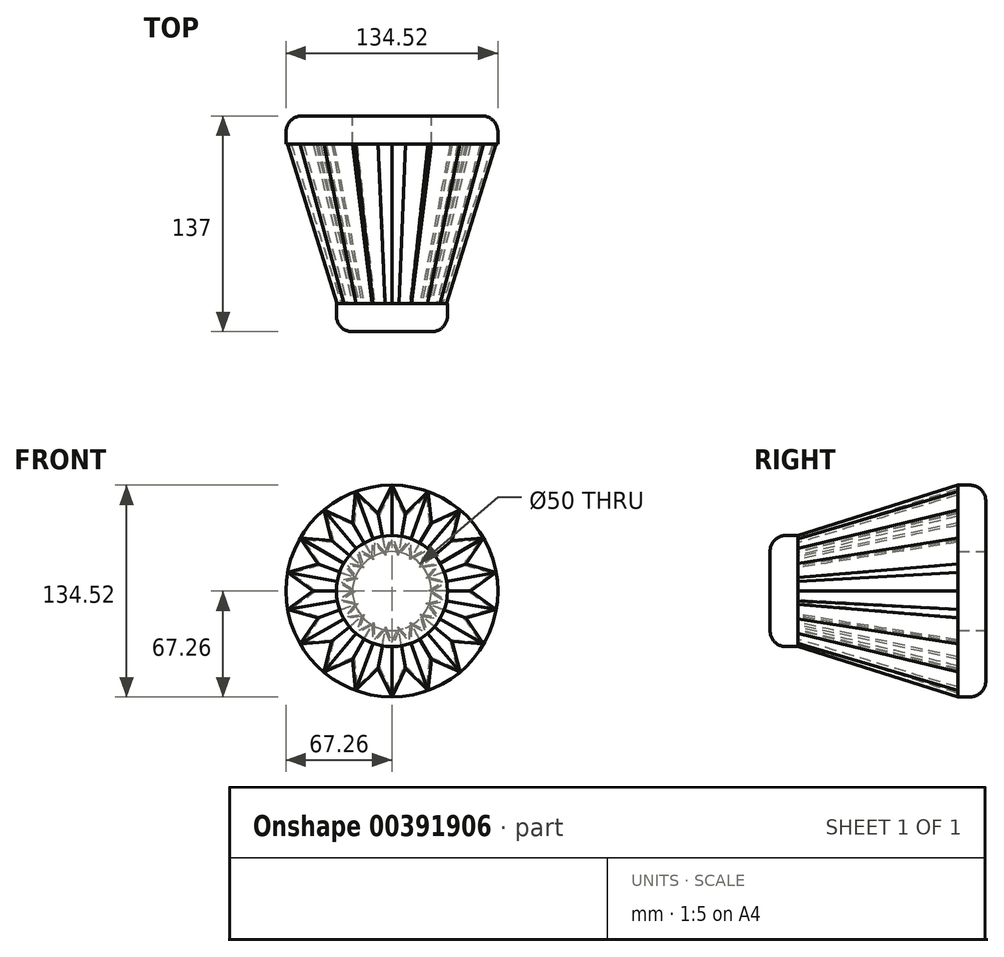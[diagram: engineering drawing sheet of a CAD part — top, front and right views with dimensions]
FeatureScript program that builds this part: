
annotation { "Feature Type Name" : "Feature", "Feature Type Description" : "" }
export const myFeature = defineFeature(function(context is Context, id is Id, definition is map)
    precondition{}
    {
        {
            var Q0;
            Q0=qCreatedBy(makeId("Front.planeOp"),FACE);
            var sketch = newSketch(context, id + "F0", { "sketchPlane" : qUnion([Q0])});
            skLineSegment(sketch, "E0", {"start": v(0, 0) * mm, "end": v(0, 67.26) * mm, "construction": true});
            skLineSegment(sketch, "E1", {"start": v(0, 0) * mm, "end": v(-8.68, 49.24) * mm});
            skLineSegment(sketch, "E2", {"start": v(-8.68, 49.24) * mm, "end": v(0, 67.26) * mm});
            skLineSegment(sketch, "E3.MirrorCS", {"start": v(8.68, 49.24) * mm, "end": v(0, 67.26) * mm});
            skLineSegment(sketch, "E4.MirrorCS", {"start": v(0, 0) * mm, "end": v(8.68, 49.24) * mm});
            skSolve(sketch);
        }
        {
            var Q0;
            Q0=qCreatedBy(makeId("Front.planeOp"),FACE);
            cPlane(context, id + "F1", {"entities" : qUnion([Q0]), "cplaneType" : CPlaneType.OFFSET, "offset" : 101.5 * mm, "width" : 150 * mm, "height" : 150 * mm});
        }
        {
            var Q0;
            Q0=qCreatedBy(id+"F1.planeOp",FACE);
            var sketch = newSketch(context, id + "F2", { "sketchPlane" : qUnion([Q0])});
            skLineSegment(sketch, "E5", {"start": v(0, 0) * mm, "end": v(0, 49.56) * mm, "construction": true});
            skLineSegment(sketch, "E6", {"start": v(0, 0) * mm, "end": v(-4.34, 24.62) * mm});
            skLineSegment(sketch, "E7", {"start": v(-4.34, 24.62) * mm, "end": v(0, 35.27) * mm});
            skLineSegment(sketch, "E8.MirrorCS", {"start": v(4.34, 24.62) * mm, "end": v(0, 35.27) * mm});
            skLineSegment(sketch, "E9.MirrorCS", {"start": v(0, 0) * mm, "end": v(4.34, 24.62) * mm});
            skSolve(sketch);
        }
        {
            var Q0;
            Q0=makeQuery(id+"F0.imprint","IMPRINT",FACE,{"disambiguationData":[TD([[makeQuery(id+"F0.imprint","IMPRINT",EDGE,{"derivedFrom":sQuery(id+"F0.wireOp",EDGE,"E1")}),-1.0]])]});
            var Q1;
            Q1=makeQuery(id+"F2.imprint","IMPRINT",FACE,{"disambiguationData":[TD([[makeQuery(id+"F2.imprint","IMPRINT",EDGE,{"derivedFrom":sQuery(id+"F2.wireOp",EDGE,"E6")}),-1.0]])]});
            loft(context, id + "F3", {"sheetProfilesArray" : [{ "sheetProfileEntities" : qUnion([Q0]) }, { "sheetProfileEntities" : qUnion([Q1]) }]});
        }
        {
            var Q0;
            Q0=makeQuery(id+"F3.opLoft","SWEPT_BODY",BODY,{"disambiguationData":[OSD([makeQuery(id+"F0.imprint","IMPRINT",FACE,{"disambiguationData":[TD([[makeQuery(id+"F0.imprint","IMPRINT",EDGE,{"derivedFrom":sQuery(id+"F0.wireOp",EDGE,"E1")}),-1.0]])]}),makeQuery(id+"F2.imprint","IMPRINT",FACE,{"disambiguationData":[TD([[makeQuery(id+"F2.imprint","IMPRINT",EDGE,{"derivedFrom":sQuery(id+"F2.wireOp",EDGE,"E6")}),-1.0]])]})])]});
            var Q1;
            Q1=makeQuery(id+"F3.opLoft","SWEPT_EDGE",EDGE,{"disambiguationData":[OSD([sQuery(id+"F0.wireOp",EDGE,"E1"),sQuery(id+"F0.wireOp",EDGE,"E4.MirrorCS"),sQuery(id+"F2.wireOp",EDGE,"E6"),sQuery(id+"F2.wireOp",EDGE,"E9.MirrorCS")])]});
            circularPattern(context, id + "F4", {"operationType" : NewBodyOperationType.ADD, "entities" : qUnion([Q0]), "axis" : qUnion([Q1]), "angle" : 360 * degree, "instanceCount" : 18, "equalSpace" : true});
        }
        {
            var Q0;
            {var subQ0=makeQuery(id+"F3.opLoft","CAP_FACE",FACE,{"disambiguationData":[OSD([makeQuery(id+"F2.imprint","IMPRINT",FACE,{"disambiguationData":[TD([[makeQuery(id+"F2.imprint","IMPRINT",EDGE,{"derivedFrom":sQuery(id+"F2.wireOp",EDGE,"E6")}),-1.0]])]})])],"isStart":true});Q0=makeQuery(id+"FTp9U8mSMzo62uv_1.opBoolean","MERGE",FACE,{"derivedFrom":[subQ0,makeQuery(id+"F4.opPattern","COPY",FACE,{"derivedFrom":subQ0,"instanceName":"1"}),makeQuery(id+"F4.opPattern","COPY",FACE,{"derivedFrom":subQ0,"instanceName":"2"}),makeQuery(id+"F4.opPattern","COPY",FACE,{"derivedFrom":subQ0,"instanceName":"3"}),makeQuery(id+"F4.opPattern","COPY",FACE,{"derivedFrom":subQ0,"instanceName":"4"}),makeQuery(id+"F4.opPattern","COPY",FACE,{"derivedFrom":subQ0,"instanceName":"5"}),makeQuery(id+"F4.opPattern","COPY",FACE,{"derivedFrom":subQ0,"instanceName":"6"}),makeQuery(id+"F4.opPattern","COPY",FACE,{"derivedFrom":subQ0,"instanceName":"7"}),makeQuery(id+"F4.opPattern","COPY",FACE,{"derivedFrom":subQ0,"instanceName":"8"}),makeQuery(id+"F4.opPattern","COPY",FACE,{"derivedFrom":subQ0,"instanceName":"9"}),makeQuery(id+"F4.opPattern","COPY",FACE,{"derivedFrom":subQ0,"instanceName":"10"}),makeQuery(id+"F4.opPattern","COPY",FACE,{"derivedFrom":subQ0,"instanceName":"11"}),makeQuery(id+"F4.opPattern","COPY",FACE,{"derivedFrom":subQ0,"instanceName":"12"}),makeQuery(id+"F4.opPattern","COPY",FACE,{"derivedFrom":subQ0,"instanceName":"13"}),makeQuery(id+"F4.opPattern","COPY",FACE,{"derivedFrom":subQ0,"instanceName":"14"}),makeQuery(id+"F4.opPattern","COPY",FACE,{"derivedFrom":subQ0,"instanceName":"15"}),makeQuery(id+"F4.opPattern","COPY",FACE,{"derivedFrom":subQ0,"instanceName":"16"}),makeQuery(id+"F4.opPattern","COPY",FACE,{"derivedFrom":subQ0,"instanceName":"17"})]});}
            var Q1;
            {var subQ0=makeQuery(id+"F3.opLoft","CAP_FACE",FACE,{"disambiguationData":[OSD([makeQuery(id+"F0.imprint","IMPRINT",FACE,{"disambiguationData":[TD([[makeQuery(id+"F0.imprint","IMPRINT",EDGE,{"derivedFrom":sQuery(id+"F0.wireOp",EDGE,"E1")}),-1.0]])]})])],"isStart":true});Q1=makeQuery(id+"FTp9U8mSMzo62uv_1.opBoolean","MERGE",FACE,{"derivedFrom":[subQ0,makeQuery(id+"F4.opPattern","COPY",FACE,{"derivedFrom":subQ0,"instanceName":"1"}),makeQuery(id+"F4.opPattern","COPY",FACE,{"derivedFrom":subQ0,"instanceName":"2"}),makeQuery(id+"F4.opPattern","COPY",FACE,{"derivedFrom":subQ0,"instanceName":"3"}),makeQuery(id+"F4.opPattern","COPY",FACE,{"derivedFrom":subQ0,"instanceName":"4"}),makeQuery(id+"F4.opPattern","COPY",FACE,{"derivedFrom":subQ0,"instanceName":"5"}),makeQuery(id+"F4.opPattern","COPY",FACE,{"derivedFrom":subQ0,"instanceName":"6"}),makeQuery(id+"F4.opPattern","COPY",FACE,{"derivedFrom":subQ0,"instanceName":"7"}),makeQuery(id+"F4.opPattern","COPY",FACE,{"derivedFrom":subQ0,"instanceName":"8"}),makeQuery(id+"F4.opPattern","COPY",FACE,{"derivedFrom":subQ0,"instanceName":"9"}),makeQuery(id+"F4.opPattern","COPY",FACE,{"derivedFrom":subQ0,"instanceName":"10"}),makeQuery(id+"F4.opPattern","COPY",FACE,{"derivedFrom":subQ0,"instanceName":"11"}),makeQuery(id+"F4.opPattern","COPY",FACE,{"derivedFrom":subQ0,"instanceName":"12"}),makeQuery(id+"F4.opPattern","COPY",FACE,{"derivedFrom":subQ0,"instanceName":"13"}),makeQuery(id+"F4.opPattern","COPY",FACE,{"derivedFrom":subQ0,"instanceName":"14"}),makeQuery(id+"F4.opPattern","COPY",FACE,{"derivedFrom":subQ0,"instanceName":"15"}),makeQuery(id+"F4.opPattern","COPY",FACE,{"derivedFrom":subQ0,"instanceName":"16"}),makeQuery(id+"F4.opPattern","COPY",FACE,{"derivedFrom":subQ0,"instanceName":"17"})]});}
            shell(context, id + "F5", {"entities" : qUnion([Q0, Q1]), "thickness" : 1 * mm});
        }
        {
            var Q0;
            Q0=qCreatedBy(makeId("Front.planeOp"),FACE);
            var sketch = newSketch(context, id + "F6", { "sketchPlane" : qUnion([Q0])});
            skCircle(sketch, "E10", {"center": v(0, 0) * mm, "radius": 67.26 * mm});
            skSolve(sketch);
        }
        {
            var Q0;
            Q0=qSketchRegion(id+"F6",true);
            extrude(context, id + "F7", {"entities" : qUnion([Q0]), "oppositeDirection" : true, "depth" : 17.75 * mm});
        }
        {
            var Q0;
            Q0=qCreatedBy(id+"F1.planeOp",FACE);
            var sketch = newSketch(context, id + "F8", { "sketchPlane" : qUnion([Q0])});
            skCircle(sketch, "E11", {"center": v(0, 0) * mm, "radius": 35.27 * mm});
            skSolve(sketch);
        }
        {
            var Q0;
            Q0=qSketchRegion(id+"F8",true);
            extrude(context, id + "F9", {"entities" : qUnion([Q0]), "depth" : 17.75 * mm});
        }
        {
            var Q0;
            Q0=makeQuery(id+"F9.opExtrude","CAP_EDGE",EDGE,{"disambiguationData":[OSD([sQuery(id+"F8.wireOp",EDGE,"E11")])],"isStart":false});
            var Q1;
            Q1=makeQuery(id+"F7.opExtrude","CAP_EDGE",EDGE,{"disambiguationData":[OSD([sQuery(id+"F6.wireOp",EDGE,"E10")])],"isStart":false});
            fillet(context, id + "F10", {"entities" : qUnion([Q0, Q1]), "radius" : 10 * mm, "tangentPropagation" : true, "allowEdgeOverflow" : false});
        }
        {
            var Q0;
            Q0=makeQuery(id+"F7.opExtrude","CAP_FACE",FACE,{"disambiguationData":[OSD([sQuery(id+"F6.wireOp",EDGE,"E10")])],"isStart":false});
            var sketch = newSketch(context, id + "F11", { "sketchPlane" : qUnion([Q0])});
            skCircle(sketch, "E12", {"center": v(0, 0) * mm, "radius": 25 * mm});
            skSolve(sketch);
        }
        {
            var Q0;
            Q0=makeQuery(id+"F11.imprint","IMPRINT",FACE,{"disambiguationData":[TD([[makeQuery(id+"F11.imprint","IMPRINT",EDGE,{"derivedFrom":sQuery(id+"F11.wireOp",EDGE,"E12")}),1.0]])]});
            extrude(context, id + "F12", {"entities" : qUnion([Q0]), "operationType" : NewBodyOperationType.REMOVE, "oppositeDirection" : true, "depth" : 17.8 * mm});
        }
    });
